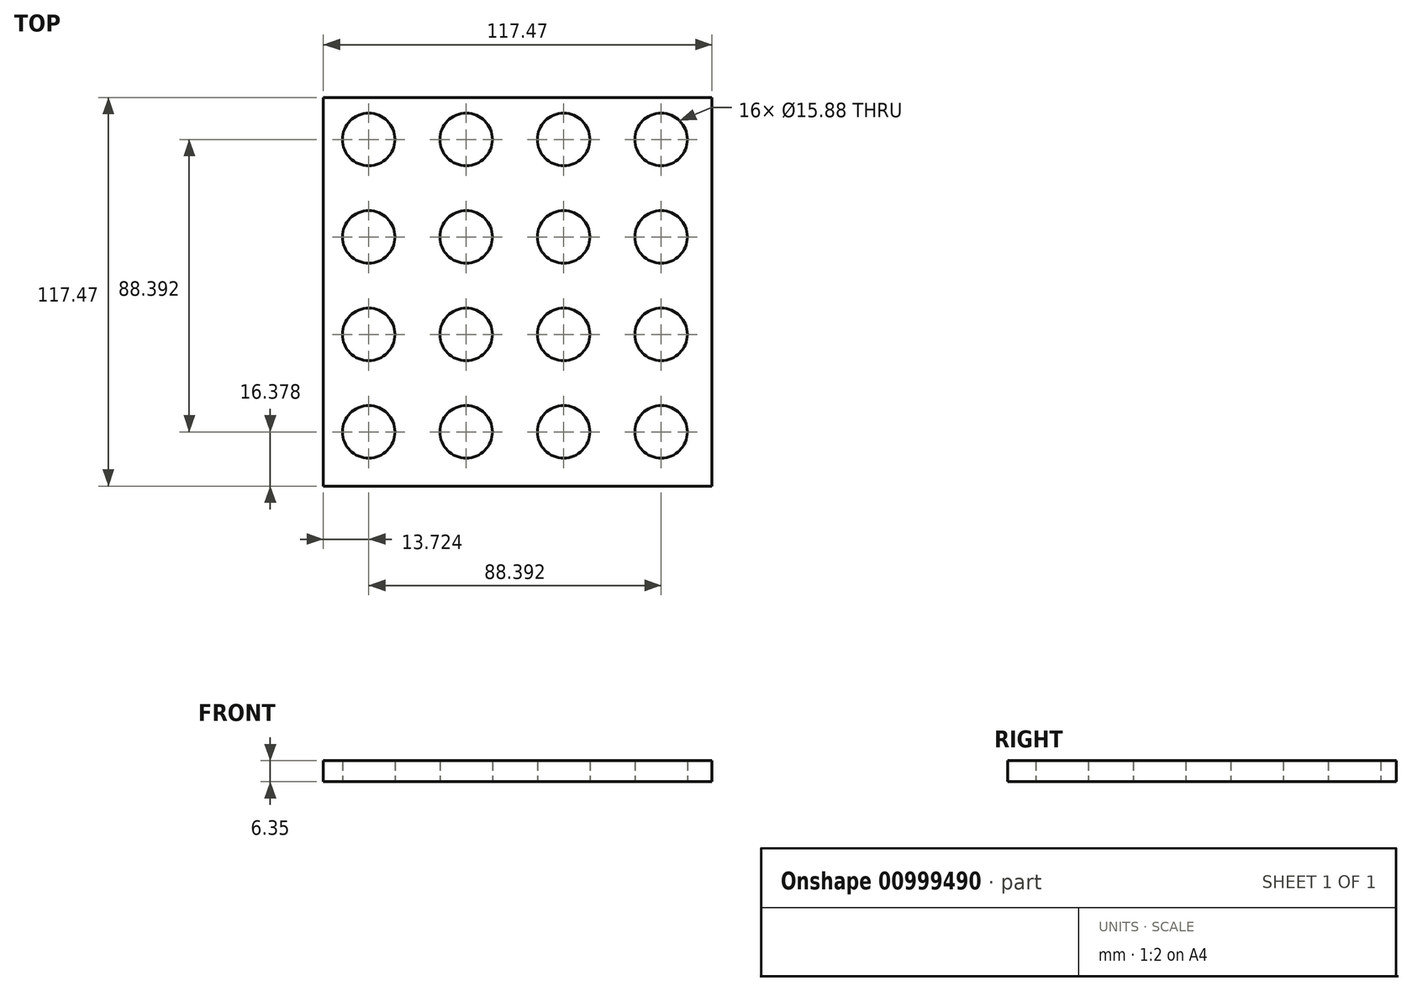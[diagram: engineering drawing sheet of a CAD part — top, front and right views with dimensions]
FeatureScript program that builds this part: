
annotation { "Feature Type Name" : "Feature", "Feature Type Description" : "" }
export const myFeature = defineFeature(function(context is Context, id is Id, definition is map)
    precondition{}
    {
        {
            var Q0;
            Q0=qCreatedBy(makeId("Top.planeOp"),FACE);
            var sketch = newSketch(context, id + "F0", { "sketchPlane" : qUnion([Q0])});
            skLineSegment(sketch, "E0.bottom", {"start": v(-58.4, 68.07) * mm, "end": v(59.08, 68.07) * mm});
            skLineSegment(sketch, "E0.top", {"start": v(-58.4, -49.4) * mm, "end": v(59.08, -49.4) * mm});
            skLineSegment(sketch, "E0.left", {"start": v(-58.4, 68.07) * mm, "end": v(-58.4, -49.4) * mm});
            skLineSegment(sketch, "E0.right", {"start": v(59.08, 68.07) * mm, "end": v(59.08, -49.4) * mm});
            skCircle(sketch, "E1", {"center": v(-44.67, 55.37) * mm, "radius": 7.94 * mm});
            skCircle(sketch, "E2.0.1.0", {"center": v(-44.67, 25.9) * mm, "radius": 7.94 * mm});
            skCircle(sketch, "E2.0.2.0", {"center": v(-44.67, -3.56) * mm, "radius": 7.94 * mm});
            skCircle(sketch, "E2.0.3.0", {"center": v(-44.67, -33.02) * mm, "radius": 7.94 * mm});
            skCircle(sketch, "E2.1.0.0", {"center": v(-15.2, 55.37) * mm, "radius": 7.94 * mm});
            skCircle(sketch, "E2.1.1.0", {"center": v(-15.2, 25.9) * mm, "radius": 7.94 * mm});
            skCircle(sketch, "E2.1.2.0", {"center": v(-15.2, -3.56) * mm, "radius": 7.94 * mm});
            skCircle(sketch, "E2.1.3.0", {"center": v(-15.2, -33.02) * mm, "radius": 7.94 * mm});
            skCircle(sketch, "E2.2.0.0", {"center": v(14.26, 55.37) * mm, "radius": 7.94 * mm});
            skCircle(sketch, "E2.2.1.0", {"center": v(14.26, 25.9) * mm, "radius": 7.94 * mm});
            skCircle(sketch, "E2.2.2.0", {"center": v(14.26, -3.56) * mm, "radius": 7.94 * mm});
            skCircle(sketch, "E2.2.3.0", {"center": v(14.26, -33.02) * mm, "radius": 7.94 * mm});
            skCircle(sketch, "E2.3.0.0", {"center": v(43.73, 55.37) * mm, "radius": 7.94 * mm});
            skCircle(sketch, "E2.3.1.0", {"center": v(43.73, 25.9) * mm, "radius": 7.94 * mm});
            skCircle(sketch, "E2.3.2.0", {"center": v(43.73, -3.56) * mm, "radius": 7.94 * mm});
            skCircle(sketch, "E2.3.3.0", {"center": v(43.73, -33.02) * mm, "radius": 7.94 * mm});
            skLineSegment(sketch, "E2.direction1", {"start": v(-44.67, 55.37) * mm, "end": v(-15.2, 55.37) * mm, "construction": true});
            skLineSegment(sketch, "E2.direction2", {"start": v(-44.67, 55.37) * mm, "end": v(-44.67, 25.9) * mm, "construction": true});
            skSolve(sketch);
        }
        {
            var Q0;
            Q0=makeQuery(id+"F0.imprint","IMPRINT",FACE,{"disambiguationData":[TD([[makeQuery(id+"F0.imprint","IMPRINT",EDGE,{"derivedFrom":sQuery(id+"F0.wireOp",EDGE,"E0.bottom")}),-1.0]])]});
            extrude(context, id + "F1", {"entities" : qUnion([Q0]), "depth" : 6.35 * mm, "offsetDistance" : 25.4 * mm});
        }
    });
